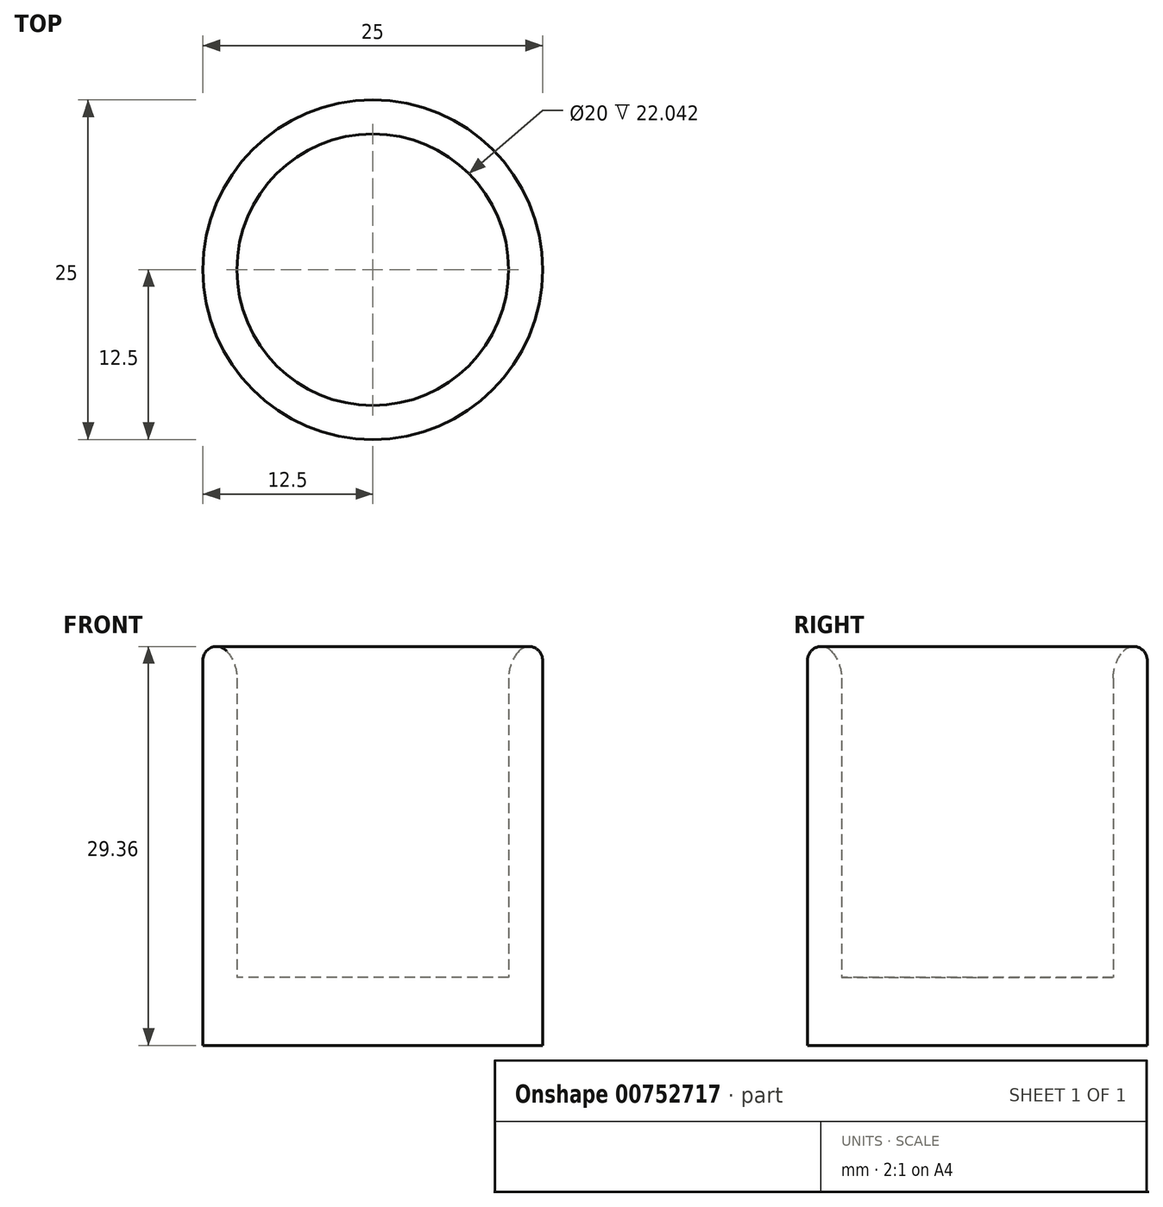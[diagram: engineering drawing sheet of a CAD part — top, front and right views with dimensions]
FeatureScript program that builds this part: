
annotation { "Feature Type Name" : "Feature", "Feature Type Description" : "" }
export const myFeature = defineFeature(function(context is Context, id is Id, definition is map)
    precondition{}
    {
        {
            var Q0;
            Q0=qCreatedBy(makeId("Top.planeOp"),FACE);
            var sketch = newSketch(context, id + "F0", { "sketchPlane" : qUnion([Q0])});
            skCircle(sketch, "E0", {"center": v(0, 0) * mm, "radius": 12.5 * mm});
            skCircle(sketch, "E1", {"center": v(0, 0) * mm, "radius": 10 * mm});
            skSolve(sketch);
        }
        {
            var Q0;
            Q0=makeQuery(id+"F0.imprint","IMPRINT",FACE,{"disambiguationData":[TD([[makeQuery(id+"F0.imprint","IMPRINT",EDGE,{"derivedFrom":sQuery(id+"F0.wireOp",EDGE,"E1")}),1.0]])]});
            extrude(context, id + "F1", {"entities" : qUnion([Q0]), "depth" : 5 * mm, "offsetDistance" : 25 * mm});
        }
        {
            var Q0;
            Q0 = qSketchRegion(id + "F0", true);
            extrude(context, id + "F2", {"entities" : qUnion([Q0]), "operationType" : NewBodyOperationType.ADD, "depth" : 30 * mm, "offsetDistance" : 25 * mm});
        }
        {
            var Q0;
            Q0=makeQuery(id+"F2.opExtrude","CAP_EDGE",EDGE,{"disambiguationData":[OSD([sQuery(id+"F0.wireOp",EDGE,"E1")])],"isStart":false});
            fillet(context, id + "F3", {"entities" : qUnion([Q0]), "radius" : 3 * mm, "tangentPropagation" : true, "allowEdgeOverflow" : false});
        }
        {
            var Q0;
            Q0=makeQuery(id+"F3.opFillet","BLEND_EDGE",EDGE,{"blendedFrom":[makeQuery(id+"F2.opExtrude","CAP_EDGE",EDGE,{"disambiguationData":[OSD([sQuery(id+"F0.wireOp",EDGE,"E1")])],"isStart":false}),makeQuery(id+"F2.opExtrude","SWEPT_FACE",FACE,{"disambiguationData":[OSD([sQuery(id+"F0.wireOp",EDGE,"E0")])]})],"blendedInto":[makeQuery(id+"F2.opExtrude","SWEPT_FACE",FACE,{"disambiguationData":[OSD([sQuery(id+"F0.wireOp",EDGE,"E0")])]})]});
            fillet(context, id + "F4", {"entities" : qUnion([Q0]), "radius" : 1 * mm, "tangentPropagation" : true, "allowEdgeOverflow" : false});
        }
    });
